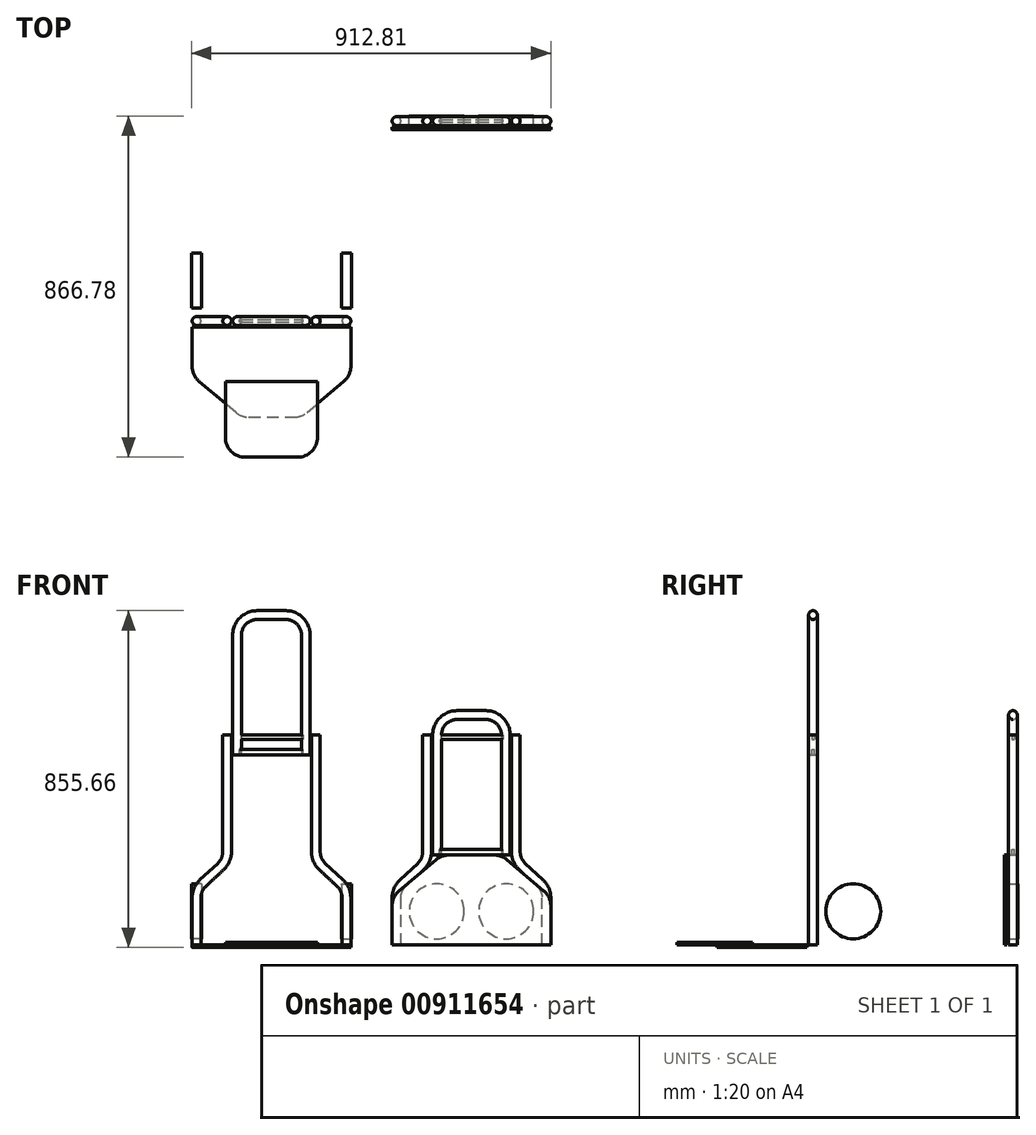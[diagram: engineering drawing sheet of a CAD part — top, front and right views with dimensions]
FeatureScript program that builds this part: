
annotation { "Feature Type Name" : "Feature", "Feature Type Description" : "" }
export const myFeature = defineFeature(function(context is Context, id is Id, definition is map)
    precondition{}
    {
        {
            var Q0;
            Q0=qCreatedBy(makeId("Front.planeOp"),FACE);
            var sketch = newSketch(context, id + "F0", { "sketchPlane" : qUnion([Q0])});
            skLineSegment(sketch, "E0", {"start": v(-87.31, 0) * mm, "end": v(-87.31, 304.8) * mm});
            skLineSegment(sketch, "E1", {"start": v(-36.51, 355.6) * mm, "end": v(36.51, 355.6) * mm});
            skLineSegment(sketch, "E2", {"start": v(87.31, 304.8) * mm, "end": v(87.31, 0) * mm});
            skPoint(sketch, "E3.visualSharp", {"position": v(87.31, 355.6) * mm});
            skArc(sketch, "E3.filletArc", {"start": v(87.31, 304.8) * mm, "mid": v(72.43, 340.72) * mm, "end": v(36.51, 355.6) * mm});
            skPoint(sketch, "E4.visualSharp", {"position": v(-87.31, 355.6) * mm});
            skArc(sketch, "E4.filletArc", {"start": v(-36.51, 355.6) * mm, "mid": v(-72.43, 340.72) * mm, "end": v(-87.31, 304.8) * mm});
            skLineSegment(sketch, "E5", {"start": v(-112.71, 304.9) * mm, "end": v(-112.71, 8.2) * mm});
            skLineSegment(sketch, "E6", {"start": v(-128.74, -28.83) * mm, "end": v(-174.47, -71.76) * mm});
            skLineSegment(sketch, "E7", {"start": v(-190.5, -108.8) * mm, "end": v(-190.5, -228.6) * mm});
            skCircle(sketch, "E8", {"center": v(-88.26, -143.16) * mm, "radius": 69.85 * mm});
            skPoint(sketch, "E8.centerSnap0", {"position": v(-190.5, -143.16) * mm});
            skLineSegment(sketch, "E9", {"start": v(0, 0) * mm, "end": v(0, -228.6) * mm, "construction": true});
            skPoint(sketch, "E10.orphan", {"position": v(-190.5, -199.51) * mm});
            skLineSegment(sketch, "E11", {"start": v(0, -228.6) * mm, "end": v(-216.38, -228.6) * mm, "construction": true});
            skPoint(sketch, "E12.visualSharp", {"position": v(-112.71, -13.78) * mm});
            skArc(sketch, "E12.filletArc", {"start": v(-128.74, -28.83) * mm, "mid": v(-116.9, -11.97) * mm, "end": v(-112.71, 8.2) * mm});
            skPoint(sketch, "E13.visualSharp", {"position": v(-190.5, -86.8) * mm});
            skArc(sketch, "E13.filletArc", {"start": v(-174.47, -71.76) * mm, "mid": v(-186.32, -88.61) * mm, "end": v(-190.5, -108.8) * mm});
            skLineSegment(sketch, "E14.bottom", {"start": v(-81.32, 0) * mm, "end": v(79.74, 0) * mm});
            skLineSegment(sketch, "E14.top", {"start": v(-81.32, 14.3) * mm, "end": v(79.74, 14.3) * mm});
            skLineSegment(sketch, "E14.left", {"start": v(-81.32, 0) * mm, "end": v(-81.32, 14.3) * mm});
            skLineSegment(sketch, "E14.right", {"start": v(79.74, 0) * mm, "end": v(79.74, 14.3) * mm});
            skLineSegment(sketch, "E15.bottom", {"start": v(-76.99, 304.8) * mm, "end": v(79.74, 304.8) * mm});
            skLineSegment(sketch, "E15.top", {"start": v(-76.99, 293.07) * mm, "end": v(79.74, 293.07) * mm});
            skLineSegment(sketch, "E15.left", {"start": v(-76.99, 304.8) * mm, "end": v(-76.99, 293.07) * mm});
            skLineSegment(sketch, "E15.right", {"start": v(79.74, 304.8) * mm, "end": v(79.74, 293.07) * mm});
            skSolve(sketch);
        }
        {
            var Q0;
            Q0=qCreatedBy(makeId("Top.planeOp"),FACE);
            var sketch = newSketch(context, id + "F1", { "sketchPlane" : qUnion([Q0])});
            skPoint(sketch, "E16.0", {"position": v(-87.31, 0) * mm});
            skCircle(sketch, "E17", {"center": v(-87.31, 0) * mm, "radius": 11.11 * mm});
            skSolve(sketch);
        }
        {
            var Q0;
            Q0=qCreatedBy(makeId("Top.planeOp"),FACE);
            var Q1;
            Q1=sQuery(id+"F0.wireOp",VERTEX,"E7.end");
            cPlane(context, id + "F2", {"entities" : qUnion([Q0, Q1]), "cplaneType" : CPlaneType.PLANE_POINT, "offset" : 25.4 * mm, "width" : 152.4 * mm, "height" : 152.4 * mm});
        }
        {
            var Q0;
            Q0=qCreatedBy(id+"F2.planeOp",FACE);
            var sketch = newSketch(context, id + "F3", { "sketchPlane" : qUnion([Q0])});
            skPoint(sketch, "E18.0", {"position": v(-190.5, 0) * mm});
            skCircle(sketch, "E19", {"center": v(-190.5, 0) * mm, "radius": 11.11 * mm});
            skSolve(sketch);
        }
        {
            var Q0;
            Q0=makeQuery(id+"F1.imprint","IMPRINT",FACE,{"disambiguationData":[TD([[makeQuery(id+"F1.imprint","IMPRINT",EDGE,{"derivedFrom":sQuery(id+"F1.wireOp",EDGE,"E17")}),1.0]])]});
            var Q1;
            Q1=sQuery(id+"F0.wireOp",EDGE,"E0");
            var Q2;
            Q2=sQuery(id+"F0.wireOp",EDGE,"E4.filletArc");
            var Q3;
            Q3=sQuery(id+"F0.wireOp",EDGE,"E1");
            var Q4;
            Q4=sQuery(id+"F0.wireOp",EDGE,"E3.filletArc");
            var Q5;
            Q5=sQuery(id+"F0.wireOp",EDGE,"E2");
            sweep(context, id + "F4", {"profiles" : qUnion([Q0]), "path" : qUnion([Q1, Q2, Q3, Q4, Q5])});
        }
        {
            var Q0;
            Q0=makeQuery(id+"F3.imprint","IMPRINT",FACE,{"disambiguationData":[TD([[makeQuery(id+"F3.imprint","IMPRINT",EDGE,{"derivedFrom":sQuery(id+"F3.wireOp",EDGE,"E19")}),1.0]])]});
            var Q1;
            Q1=sQuery(id+"F0.wireOp",EDGE,"E7");
            var Q2;
            Q2=sQuery(id+"F0.wireOp",EDGE,"E13.filletArc");
            var Q3;
            Q3=sQuery(id+"F0.wireOp",EDGE,"E6");
            var Q4;
            Q4=sQuery(id+"F0.wireOp",EDGE,"E12.filletArc");
            var Q5;
            Q5=sQuery(id+"F0.wireOp",EDGE,"E5");
            sweep(context, id + "F5", {"profiles" : qUnion([Q0]), "path" : qUnion([Q1, Q2, Q3, Q4, Q5])});
        }
        {
            var Q0;
            Q0=makeQuery(id+"F0.imprint","IMPRINT",FACE,{"disambiguationData":[TD([[makeQuery(id+"F0.imprint","IMPRINT",EDGE,{"derivedFrom":sQuery(id+"F0.wireOp",EDGE,"E8")}),1.0]])]});
            extrude(context, id + "F6", {"entities" : qUnion([Q0]), "endBound" : BoundingType.SYMMETRIC, "depth" : 25.4 * mm, "offsetDistance" : 25.4 * mm});
        }
        {
            var Q0;
            Q0=makeQuery(id+"F6.opExtrude","SWEPT_BODY",BODY,{"disambiguationData":[OSD([sQuery(id+"F0.wireOp",EDGE,"E8")])]});
            var Q1;
            Q1=makeQuery(id+"F5.opSweep","SWEPT_BODY",BODY,{"disambiguationData":[OSD([sQuery(id+"F0.wireOp",EDGE,"E5"),sQuery(id+"F3.wireOp",EDGE,"E19")])]});
            var Q2;
            Q2=qCreatedBy(makeId("Right.planeOp"),FACE);
            mirror(context, id + "F7", {"entities" : qUnion([Q0, Q1]), "mirrorPlane" : qUnion([Q2])});
        }
        {
            var Q0;
            Q0=makeQuery(id+"F7.opPattern","COPY",FACE,{"derivedFrom":makeQuery(id+"F6.opExtrude","CAP_FACE",FACE,{"disambiguationData":[OSD([sQuery(id+"F0.wireOp",EDGE,"E8")])],"isStart":false}),"instanceName":"1"});
            cPlane(context, id + "F8", {"entities" : qUnion([Q0]), "cplaneType" : CPlaneType.OFFSET, "offset" : 3.17 * mm, "width" : 152.4 * mm, "height" : 152.4 * mm});
        }
        {
            var Q0;
            Q0=qCreatedBy(id+"F8.planeOp",FACE);
            var sketch = newSketch(context, id + "F9", { "sketchPlane" : qUnion([Q0])});
            skLineSegment(sketch, "E20", {"start": v(-76.2, 304.8) * mm, "end": v(-76.2, 0) * mm, "construction": true});
            skLineSegment(sketch, "E21.0", {"start": v(-98.43, 0) * mm, "end": v(-76.2, 0) * mm, "construction": true});
            skLineSegment(sketch, "E22", {"start": v(76.2, 0) * mm, "end": v(76.2, 304.8) * mm, "construction": true});
            skLineSegment(sketch, "E23", {"start": v(-123.83, 8.2) * mm, "end": v(-123.83, 304.9) * mm, "construction": true});
            skLineSegment(sketch, "E24", {"start": v(123.83, 304.9) * mm, "end": v(123.83, 8.2) * mm, "construction": true});
            skLineSegment(sketch, "E25", {"start": v(-57.62, 0) * mm, "end": v(57.62, 0) * mm});
            skLineSegment(sketch, "E26", {"start": v(90.4, -12) * mm, "end": v(183.6, -90.72) * mm});
            skLineSegment(sketch, "E27", {"start": v(-90.4, -12) * mm, "end": v(-183.6, -90.72) * mm});
            skPoint(sketch, "E28.visualSharp", {"position": v(-76.2, 0) * mm});
            skArc(sketch, "E28.filletArc", {"start": v(-57.62, 0) * mm, "mid": v(-75.07, -3.1) * mm, "end": v(-90.4, -12) * mm});
            skPoint(sketch, "E29.visualSharp", {"position": v(76.2, 0) * mm});
            skArc(sketch, "E29.filletArc", {"start": v(90.4, -12) * mm, "mid": v(75.07, -3.1) * mm, "end": v(57.62, 0) * mm});
            skPoint(sketch, "E30.visualSharp", {"position": v(-201.61, -105.94) * mm});
            skArc(sketch, "E30.filletArc", {"start": v(-183.6, -90.72) * mm, "mid": v(-196.89, -108.13) * mm, "end": v(-201.61, -129.53) * mm});
            skPoint(sketch, "E31.visualSharp", {"position": v(201.61, -105.94) * mm});
            skArc(sketch, "E31.filletArc", {"start": v(201.61, -129.53) * mm, "mid": v(196.89, -108.13) * mm, "end": v(183.6, -90.72) * mm});
            skLineSegment(sketch, "E32.0", {"start": v(-201.61, -228.6) * mm, "end": v(-179.39, -228.6) * mm});
            skLineSegment(sketch, "E33.0", {"start": v(201.61, -228.6) * mm, "end": v(179.39, -228.6) * mm});
            skLineSegment(sketch, "E34", {"start": v(-201.61, -228.6) * mm, "end": v(-201.61, -108.8) * mm});
            skLineSegment(sketch, "E35", {"start": v(201.61, -108.8) * mm, "end": v(201.61, -228.6) * mm});
            skLineSegment(sketch, "E36", {"start": v(-179.39, -228.6) * mm, "end": v(179.39, -228.6) * mm});
            skSolve(sketch);
        }
        {
            var Q0;
            Q0=makeQuery(id+"F9.imprint","IMPRINT",FACE,{"disambiguationData":[TD([[makeQuery(id+"F9.imprint","IMPRINT",EDGE,{"derivedFrom":sQuery(id+"F9.wireOp",EDGE,"E25")}),-1.0]])]});
            extrude(context, id + "F10", {"entities" : qUnion([Q0]), "depth" : 6.35 * mm, "offsetDistance" : 25.4 * mm});
        }
        {
            var Q0;
            Q0=makeQuery(id+"F0.imprint","IMPRINT",FACE,{"disambiguationData":[TD([[makeQuery(id+"F0.imprint","IMPRINT",EDGE,{"derivedFrom":sQuery(id+"F0.wireOp",EDGE,"E15.bottom")}),-1.0]])]});
            var Q1;
            Q1=makeQuery(id+"F0.imprint","IMPRINT",FACE,{"disambiguationData":[TD([[makeQuery(id+"F0.imprint","IMPRINT",EDGE,{"derivedFrom":sQuery(id+"F0.wireOp",EDGE,"E14.bottom")}),1.0]])]});
            extrude(context, id + "F11", {"entities" : qUnion([Q0, Q1]), "endBound" : BoundingType.SYMMETRIC, "depth" : 6.35 * mm, "offsetDistance" : 25.4 * mm});
        }
        {
            var Q0;
            Q0=makeQuery(id+"F7.opPattern","COPY",BODY,{"derivedFrom":makeQuery(id+"F6.opExtrude","SWEPT_BODY",BODY,{"disambiguationData":[OSD([sQuery(id+"F0.wireOp",EDGE,"E8")])]}),"instanceName":"1"});
            var Q1;
            Q1=makeQuery(id+"F6.opExtrude","SWEPT_BODY",BODY,{"disambiguationData":[OSD([sQuery(id+"F0.wireOp",EDGE,"E8")])]});
            var Q2;
            Q2=makeQuery(id+"F4.opSweep","SWEPT_BODY",BODY,{"disambiguationData":[OSD([sQuery(id+"F0.wireOp",EDGE,"E2"),sQuery(id+"F1.wireOp",EDGE,"E17")])]});
            var Q3;
            Q3=makeQuery(id+"F10.opExtrude","SWEPT_BODY",BODY,{"disambiguationData":[OSD([sQuery(id+"F9.wireOp",EDGE,"E25"),sQuery(id+"F9.wireOp",EDGE,"E26"),sQuery(id+"F9.wireOp",EDGE,"E27"),sQuery(id+"F9.wireOp",EDGE,"E28.filletArc"),sQuery(id+"F9.wireOp",EDGE,"E29.filletArc"),sQuery(id+"F9.wireOp",EDGE,"E30.filletArc"),sQuery(id+"F9.wireOp",EDGE,"E31.filletArc"),sQuery(id+"F9.wireOp",EDGE,"E32.0"),sQuery(id+"F9.wireOp",EDGE,"E33.0"),sQuery(id+"F9.wireOp",EDGE,"E34"),sQuery(id+"F9.wireOp",EDGE,"E35"),sQuery(id+"F9.wireOp",EDGE,"E36")])]});
            var Q4;
            Q4=makeQuery(id+"F7.opPattern","COPY",BODY,{"derivedFrom":makeQuery(id+"F5.opSweep","SWEPT_BODY",BODY,{"disambiguationData":[OSD([sQuery(id+"F0.wireOp",EDGE,"E5"),sQuery(id+"F3.wireOp",EDGE,"E19")])]}),"instanceName":"1"});
            var Q5;
            Q5=makeQuery(id+"F5.opSweep","SWEPT_BODY",BODY,{"disambiguationData":[OSD([sQuery(id+"F0.wireOp",EDGE,"E5"),sQuery(id+"F3.wireOp",EDGE,"E19")])]});
            var Q6;
            Q6=makeQuery(id+"F11.opExtrude","SWEPT_BODY",BODY,{"disambiguationData":[OSD([sQuery(id+"F0.wireOp",EDGE,"E15.bottom"),sQuery(id+"F0.wireOp",EDGE,"E15.top"),sQuery(id+"F0.wireOp",EDGE,"E15.left"),sQuery(id+"F0.wireOp",EDGE,"E15.right")])]});
            var Q7;
            Q7=makeQuery(id+"F11.opExtrude","SWEPT_BODY",BODY,{"disambiguationData":[OSD([sQuery(id+"F0.wireOp",EDGE,"E14.bottom"),sQuery(id+"F0.wireOp",EDGE,"E14.top"),sQuery(id+"F0.wireOp",EDGE,"E14.left"),sQuery(id+"F0.wireOp",EDGE,"E14.right")])]});
            transform(context, id + "F12", {"entities" : qUnion([Q0, Q1, Q2, Q3, Q4, Q5, Q6, Q7]), "transformType" : TransformType.TRANSLATION_3D, "dx" : 508 * mm, "dy" : 508 * mm, "dz" : 0 * mm, "makeCopy" : true});
        }
        {
            var Q0;
            Q0=makeQuery(id+"F10.opExtrude","SWEPT_BODY",BODY,{"disambiguationData":[OSD([sQuery(id+"F9.wireOp",EDGE,"E25"),sQuery(id+"F9.wireOp",EDGE,"E26"),sQuery(id+"F9.wireOp",EDGE,"E27"),sQuery(id+"F9.wireOp",EDGE,"E28.filletArc"),sQuery(id+"F9.wireOp",EDGE,"E29.filletArc"),sQuery(id+"F9.wireOp",EDGE,"E30.filletArc"),sQuery(id+"F9.wireOp",EDGE,"E31.filletArc"),sQuery(id+"F9.wireOp",EDGE,"E32.0"),sQuery(id+"F9.wireOp",EDGE,"E33.0"),sQuery(id+"F9.wireOp",EDGE,"E34"),sQuery(id+"F9.wireOp",EDGE,"E35"),sQuery(id+"F9.wireOp",EDGE,"E36")])]});
            var Q1;
            Q1=makeQuery(id+"F10.opExtrude","CAP_EDGE",EDGE,{"disambiguationData":[OSD([sQuery(id+"F9.wireOp",EDGE,"E32.0"),sQuery(id+"F9.wireOp",EDGE,"E33.0"),sQuery(id+"F9.wireOp",EDGE,"E36")])],"isStart":true});
            transform(context, id + "F13", {"entities" : qUnion([Q0]), "transformType" : TransformType.ROTATION, "transformAxis" : qUnion([Q1]), "angle" : 90 * degree, "makeCopy" : false});
        }
        {
            var Q0;
            Q0=makeQuery(id+"F6.opExtrude","SWEPT_BODY",BODY,{"disambiguationData":[OSD([sQuery(id+"F0.wireOp",EDGE,"E8")])]});
            var Q1;
            Q1=makeQuery(id+"F5.opSweep","SWEPT_FACE",FACE,{"disambiguationData":[OSD([sQuery(id+"F0.wireOp",EDGE,"E7"),sQuery(id+"F3.wireOp",EDGE,"E19")])]});
            transform(context, id + "F14", {"entities" : qUnion([Q0]), "transformType" : TransformType.ROTATION, "transformAxis" : qUnion([Q1]), "angle" : 90 * degree, "makeCopy" : false});
        }
        {
            var Q0;
            Q0=makeQuery(id+"F7.opPattern","COPY",BODY,{"derivedFrom":makeQuery(id+"F6.opExtrude","SWEPT_BODY",BODY,{"disambiguationData":[OSD([sQuery(id+"F0.wireOp",EDGE,"E8")])]}),"instanceName":"1"});
            var Q1;
            Q1=makeQuery(id+"F7.opPattern","COPY",FACE,{"derivedFrom":makeQuery(id+"F5.opSweep","SWEPT_FACE",FACE,{"disambiguationData":[OSD([sQuery(id+"F0.wireOp",EDGE,"E7"),sQuery(id+"F3.wireOp",EDGE,"E19")])]}),"instanceName":"1"});
            transform(context, id + "F15", {"entities" : qUnion([Q0]), "transformType" : TransformType.ROTATION, "transformAxis" : qUnion([Q1]), "angle" : 90 * degree, "oppositeDirection" : true, "makeCopy" : false});
        }
        {
            var Q0;
            Q0=makeQuery(id+"F4.opSweep","SWEPT_BODY",BODY,{"disambiguationData":[OSD([sQuery(id+"F0.wireOp",EDGE,"E2"),sQuery(id+"F1.wireOp",EDGE,"E17")])]});
            var Q1;
            Q1=makeQuery(id+"F11.opExtrude","SWEPT_BODY",BODY,{"disambiguationData":[OSD([sQuery(id+"F0.wireOp",EDGE,"E14.bottom"),sQuery(id+"F0.wireOp",EDGE,"E14.top"),sQuery(id+"F0.wireOp",EDGE,"E14.left"),sQuery(id+"F0.wireOp",EDGE,"E14.right")])]});
            transform(context, id + "F16", {"entities" : qUnion([Q0, Q1]), "transformType" : TransformType.TRANSLATION_3D, "dx" : 0 * mm, "dy" : 0 * mm, "dz" : 254 * mm, "makeCopy" : false});
        }
        {
            var Q0;
            Q0=makeQuery(id+"F10.opExtrude","CAP_FACE",FACE,{"disambiguationData":[OSD([sQuery(id+"F9.wireOp",EDGE,"E25"),sQuery(id+"F9.wireOp",EDGE,"E26"),sQuery(id+"F9.wireOp",EDGE,"E27"),sQuery(id+"F9.wireOp",EDGE,"E28.filletArc"),sQuery(id+"F9.wireOp",EDGE,"E29.filletArc"),sQuery(id+"F9.wireOp",EDGE,"E30.filletArc"),sQuery(id+"F9.wireOp",EDGE,"E31.filletArc"),sQuery(id+"F9.wireOp",EDGE,"E32.0"),sQuery(id+"F9.wireOp",EDGE,"E33.0"),sQuery(id+"F9.wireOp",EDGE,"E34"),sQuery(id+"F9.wireOp",EDGE,"E35"),sQuery(id+"F9.wireOp",EDGE,"E36")])],"isStart":true});
            var sketch = newSketch(context, id + "F17", { "sketchPlane" : qUnion([Q0])});
            skLineSegment(sketch, "E37.0", {"start": v(-90.4, -232.48) * mm, "end": v(-183.6, -153.76) * mm});
            skLineSegment(sketch, "E38.0", {"start": v(90.4, -232.48) * mm, "end": v(183.6, -153.76) * mm});
            skLineSegment(sketch, "E39", {"start": v(-183.6, -153.76) * mm, "end": v(183.6, -153.76) * mm});
            skLineSegment(sketch, "E40", {"start": v(-117.1, -153.76) * mm, "end": v(-117.1, -295.28) * mm});
            skLineSegment(sketch, "E41", {"start": v(-66.3, -346.08) * mm, "end": v(66, -346.08) * mm});
            skLineSegment(sketch, "E42", {"start": v(116.8, -295.28) * mm, "end": v(116.8, -153.76) * mm});
            skPoint(sketch, "E43.visualSharp", {"position": v(-117.1, -346.08) * mm});
            skArc(sketch, "E43.filletArc", {"start": v(-117.1, -295.28) * mm, "mid": v(-102.21, -331.2) * mm, "end": v(-66.3, -346.08) * mm});
            skPoint(sketch, "E44.visualSharp", {"position": v(116.8, -346.08) * mm});
            skArc(sketch, "E44.filletArc", {"start": v(66, -346.08) * mm, "mid": v(101.91, -331.2) * mm, "end": v(116.8, -295.28) * mm});
            skPoint(sketch, "E45.orphan", {"position": v(-117.1, -232.48) * mm});
            skPoint(sketch, "E46.orphan", {"position": v(116.8, -232.48) * mm});
            skSolve(sketch);
        }
        {
            var Q0;
            Q0=makeQuery(id+"F17.imprint","IMPRINT",FACE,{"disambiguationData":[TD([[makeQuery(id+"F17.imprint","IMPRINT",EDGE,{"derivedFrom":sQuery(id+"F17.wireOp",EDGE,"E41")}),1.0]])]});
            var Q1;
            Q1=makeQuery(id+"F17.imprint","IMPRINT",FACE,{"disambiguationData":[TD([[makeQuery(id+"F17.imprint","IMPRINT",EDGE,{"derivedFrom":makeQuery(id+"F10.opExtrude","CAP_EDGE",EDGE,{"disambiguationData":[OSD([sQuery(id+"F9.wireOp",EDGE,"E25")])],"isStart":true})}),1.0]])]});
            extrude(context, id + "F18", {"entities" : qUnion([Q0, Q1]), "depth" : 6.35 * mm, "offsetDistance" : 25.4 * mm});
        }
    });
